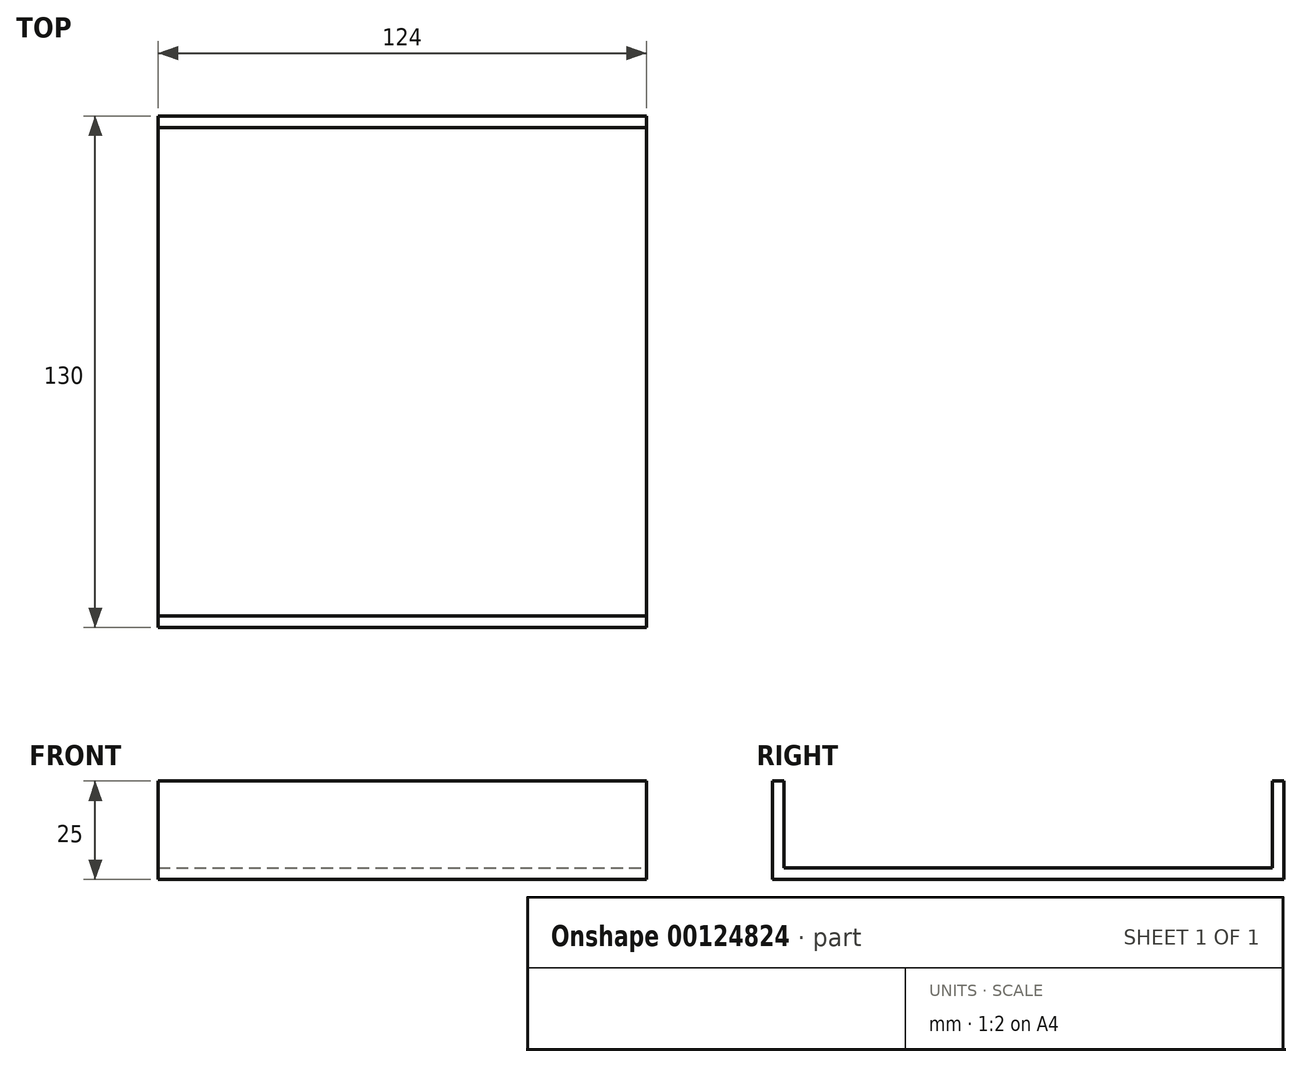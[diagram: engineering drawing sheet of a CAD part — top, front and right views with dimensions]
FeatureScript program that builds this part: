
annotation { "Feature Type Name" : "Feature", "Feature Type Description" : "" }
export const myFeature = defineFeature(function(context is Context, id is Id, definition is map)
    precondition{}
    {
        {
            var Q0;
            Q0=qCreatedBy(makeId("Top.planeOp"),FACE);
            var sketch = newSketch(context, id + "F0", { "sketchPlane" : qUnion([Q0])});
            skLineSegment(sketch, "E0.bottom", {"start": v(-50.15, 11.06) * mm, "end": v(79.85, 11.06) * mm});
            skLineSegment(sketch, "E0.top", {"start": v(-50.15, -118.94) * mm, "end": v(79.85, -118.94) * mm});
            skLineSegment(sketch, "E0.left", {"start": v(-50.15, 11.06) * mm, "end": v(-50.15, -118.94) * mm});
            skLineSegment(sketch, "E0.right", {"start": v(79.85, 11.06) * mm, "end": v(79.85, -118.94) * mm});
            skLineSegment(sketch, "E1.bottom", {"start": v(-58.81, 11.06) * mm, "end": v(-50.15, 11.06) * mm});
            skLineSegment(sketch, "E1.top", {"start": v(-58.81, -118.94) * mm, "end": v(-50.15, -118.94) * mm});
            skLineSegment(sketch, "E2.bottom", {"start": v(79.85, -118.94) * mm, "end": v(79.85, -118.94) * mm});
            skLineSegment(sketch, "E2.top", {"start": v(79.85, 11.06) * mm, "end": v(79.85, 11.06) * mm});
            skLineSegment(sketch, "E2.left", {"start": v(79.85, -118.94) * mm, "end": v(79.85, 11.06) * mm});
            skLineSegment(sketch, "E2.right", {"start": v(79.85, -118.94) * mm, "end": v(79.85, 11.06) * mm});
            skLineSegment(sketch, "E3.bottom", {"start": v(79.85, 11.06) * mm, "end": v(47.19, 11.06) * mm});
            skLineSegment(sketch, "E3.top", {"start": v(79.85, -118.94) * mm, "end": v(76.85, -118.94) * mm});
            skLineSegment(sketch, "E4.left", {"start": v(-50.15, -118.94) * mm, "end": v(-50.15, -118.94) * mm});
            skLineSegment(sketch, "E5.bottom", {"start": v(79.85, -118.94) * mm, "end": v(-50.15, -118.94) * mm});
            skLineSegment(sketch, "E5.top", {"start": v(79.85, -118.94) * mm, "end": v(-50.15, -118.94) * mm});
            skLineSegment(sketch, "E6.left", {"start": v(-50.15, -118.94) * mm, "end": v(-50.15, -116.94) * mm});
            skLineSegment(sketch, "E6.right", {"start": v(79.85, -118.94) * mm, "end": v(79.85, -116.94) * mm});
            skLineSegment(sketch, "E7.bottom", {"start": v(-50.15, 11.06) * mm, "end": v(57.85, 11.06) * mm});
            skLineSegment(sketch, "E7.left", {"start": v(-50.15, 11.06) * mm, "end": v(-50.15, 9.06) * mm});
            skLineSegment(sketch, "E8.bottom", {"start": v(-58.81, -118.94) * mm, "end": v(47.19, -118.94) * mm});
            skLineSegment(sketch, "E9.bottom", {"start": v(-58.81, 11.06) * mm, "end": v(47.19, 11.06) * mm});
            skLineSegment(sketch, "E10.bottom", {"start": v(-50.15, 11.06) * mm, "end": v(-47.15, 11.06) * mm});
            skLineSegment(sketch, "E10.top", {"start": v(-50.15, -118.94) * mm, "end": v(-47.15, -118.94) * mm});
            skLineSegment(sketch, "E10.right", {"start": v(-47.15, 11.06) * mm, "end": v(-47.15, -118.94) * mm});
            skLineSegment(sketch, "E11.bottom", {"start": v(79.85, 11.06) * mm, "end": v(76.85, 11.06) * mm});
            skLineSegment(sketch, "E11.right", {"start": v(76.85, 11.06) * mm, "end": v(76.85, -118.94) * mm});
            skLineSegment(sketch, "E12.bottom", {"start": v(-47.15, 11.06) * mm, "end": v(76.85, 11.06) * mm});
            skLineSegment(sketch, "E12.top", {"start": v(-47.15, 8.06) * mm, "end": v(76.85, 8.06) * mm});
            skLineSegment(sketch, "E12.left", {"start": v(-47.15, 11.06) * mm, "end": v(-47.15, 8.06) * mm});
            skLineSegment(sketch, "E12.right", {"start": v(76.85, 11.06) * mm, "end": v(76.85, 8.06) * mm});
            skLineSegment(sketch, "E13.bottom", {"start": v(-47.15, -118.94) * mm, "end": v(76.85, -118.94) * mm});
            skLineSegment(sketch, "E13.top", {"start": v(-47.15, -115.94) * mm, "end": v(76.85, -115.94) * mm});
            skLineSegment(sketch, "E13.left", {"start": v(-47.15, -118.94) * mm, "end": v(-47.15, -115.94) * mm});
            skLineSegment(sketch, "E13.right", {"start": v(76.85, -118.94) * mm, "end": v(76.85, -115.94) * mm});
            skSolve(sketch);
        }
        {
            var Q0;
            Q0=makeQuery(id+"F0.imprint","IMPRINT",FACE,{"disambiguationData":[TD([[makeQuery(id+"F0.imprint","IMPRINT",EDGE,{"derivedFrom":sQuery(id+"F0.wireOp",EDGE,"E12.top")}),1.0]])]});
            var Q1;
            {var subQ2=sQuery(id+"F0.wireOp",EDGE,"E10.bottom");Q1=makeQuery(id+"F0.imprint","IMPRINT",FACE,{"disambiguationData":[TD([[makeQuery(id+"F0.imprint","IMPRINT",EDGE,{"derivedFrom":subQ2}),-1.0]])]});}
            var Q2;
            Q2=makeQuery(id+"F0.imprint","IMPRINT",FACE,{"disambiguationData":[TD([[makeQuery(id+"F0.imprint","IMPRINT",EDGE,{"derivedFrom":sQuery(id+"F0.wireOp",EDGE,"E13.top")}),-1.0]])]});
            var Q3;
            {var subQ3=sQuery(id+"F0.wireOp",EDGE,"E3.top");Q3=makeQuery(id+"F0.imprint","IMPRINT",FACE,{"disambiguationData":[TD([[makeQuery(id+"F0.imprint","IMPRINT",EDGE,{"derivedFrom":subQ3}),-1.0]])]});}
            extrude(context, id + "F1", {"entities" : qUnion([Q0, Q1, Q2, Q3]), "depth" : 25 * mm});
        }
        {
            var Q0;
            Q0=makeQuery(id+"F0.imprint","IMPRINT",FACE,{"disambiguationData":[TD([[makeQuery(id+"F0.imprint","IMPRINT",EDGE,{"derivedFrom":sQuery(id+"F0.wireOp",EDGE,"E10.right")}),1.0]])]});
            extrude(context, id + "F2", {"entities" : qUnion([Q0]), "operationType" : NewBodyOperationType.ADD, "depth" : 3 * mm});
        }
    });
